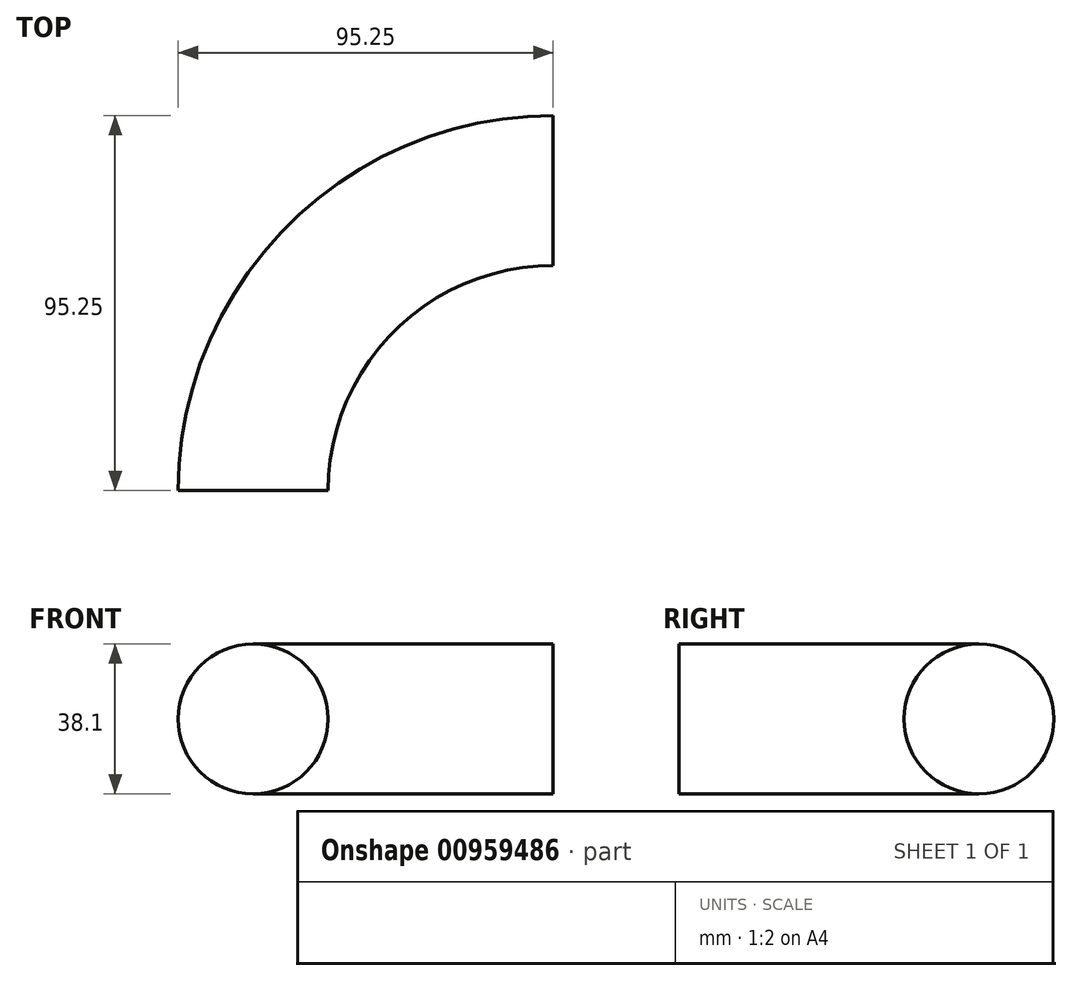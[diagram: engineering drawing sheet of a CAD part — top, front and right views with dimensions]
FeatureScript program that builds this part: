
annotation { "Feature Type Name" : "Feature", "Feature Type Description" : "" }
export const myFeature = defineFeature(function(context is Context, id is Id, definition is map)
    precondition{}
    {
        {
            var Q0;
            Q0=qCreatedBy(makeId("Front.planeOp"),FACE);
            var sketch = newSketch(context, id + "F0", { "sketchPlane" : qUnion([Q0])});
            skCircle(sketch, "E0", {"center": v(0, 0) * mm, "radius": 19.05 * mm});
            skPoint(sketch, "E1", {"position": v(0, -19.05) * mm});
            skSolve(sketch);
        }
        {
            var Q0;
            Q0=qCreatedBy(makeId("Top.planeOp"),FACE);
            var sketch = newSketch(context, id + "F1", { "sketchPlane" : qUnion([Q0])});
            skPoint(sketch, "E2", {"position": v(76.2, 0) * mm});
            skPoint(sketch, "E3", {"position": v(76.2, 76.2) * mm});
            skArc(sketch, "E4", {"start": v(76.2, 76.2) * mm, "mid": v(22.32, 53.88) * mm, "end": v(0, 0) * mm});
            skSolve(sketch);
        }
        {
            var Q0;
            Q0=makeQuery(id+"F0.imprint","IMPRINT",FACE,{"disambiguationData":[TD([[makeQuery(id+"F0.imprint","IMPRINT",EDGE,{"derivedFrom":sQuery(id+"F0.wireOp",EDGE,"E0")}),1.0]])]});
            var Q1;
            Q1=sQuery(id+"F1.wireOp",EDGE,"E4");
            sweep(context, id + "F2", {"profiles" : qUnion([Q0]), "path" : qUnion([Q1])});
        }
    });
